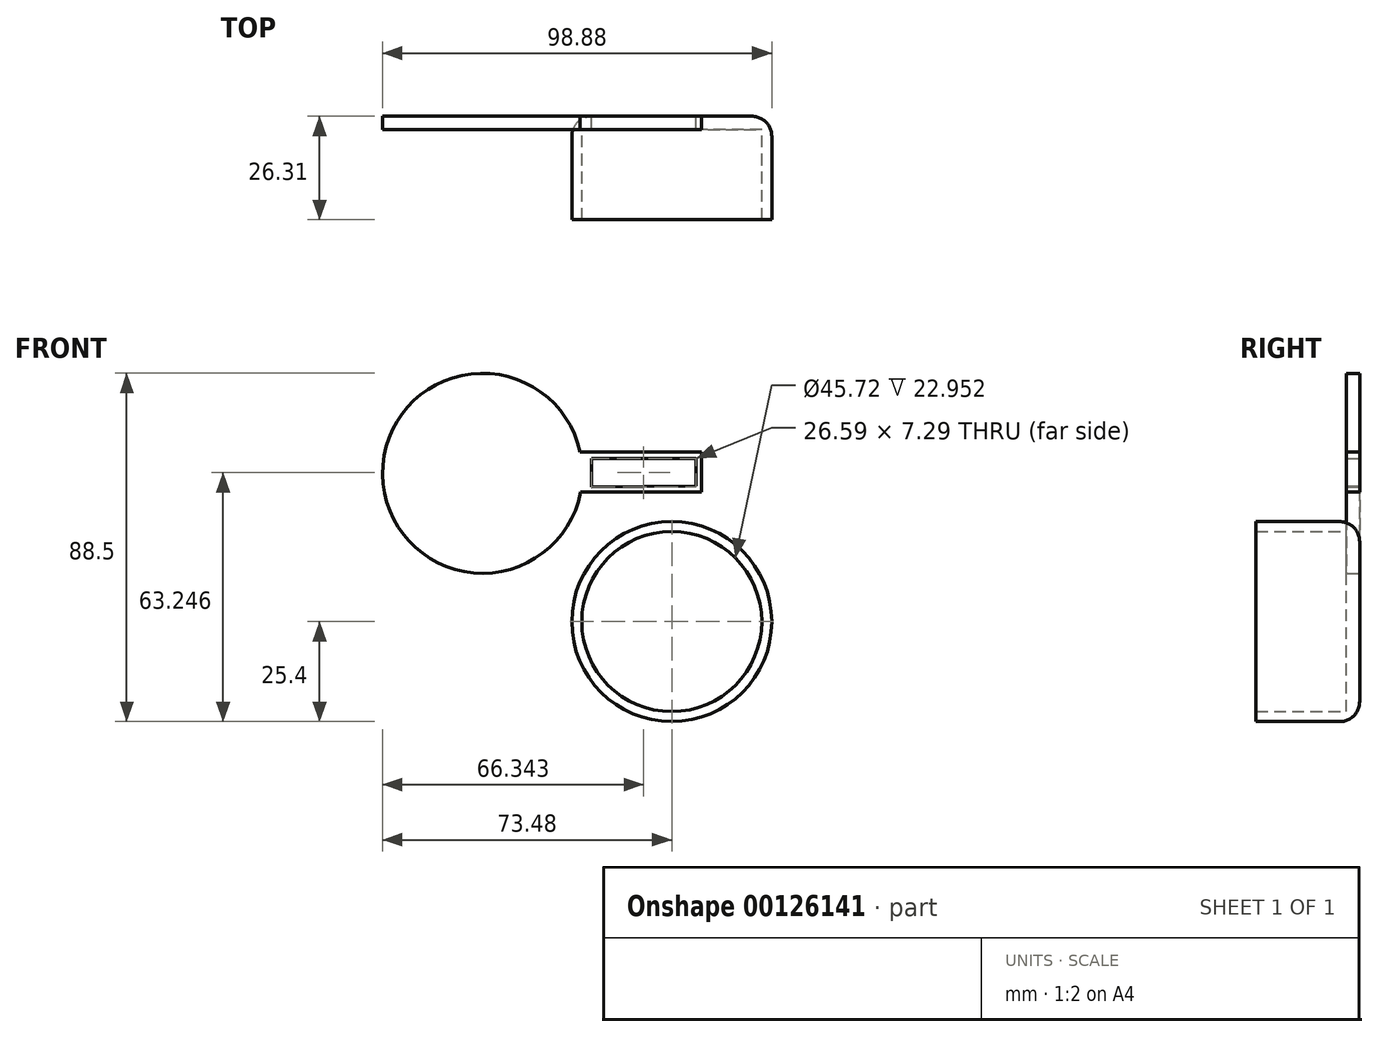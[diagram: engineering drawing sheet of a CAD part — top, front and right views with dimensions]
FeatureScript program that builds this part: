
annotation { "Feature Type Name" : "Feature", "Feature Type Description" : "" }
export const myFeature = defineFeature(function(context is Context, id is Id, definition is map)
    precondition{}
    {
        {
            var Q0;
            Q0=qCreatedBy(makeId("Front.planeOp"),FACE);
            var sketch = newSketch(context, id + "F0", { "sketchPlane" : qUnion([Q0])});
            skCircle(sketch, "E0", {"center": v(0, 0) * mm, "radius": 25.4 * mm});
            skCircle(sketch, "E1", {"center": v(-48.08, 37.7) * mm, "radius": 25.4 * mm});
            skLineSegment(sketch, "E2", {"start": v(-23.26, 43.09) * mm, "end": v(7.54, 43.09) * mm});
            skLineSegment(sketch, "E3", {"start": v(-23.14, 32.9) * mm, "end": v(7.54, 32.9) * mm});
            skLineSegment(sketch, "E4", {"start": v(7.54, 43.09) * mm, "end": v(7.54, 32.9) * mm});
            skLineSegment(sketch, "E5", {"start": v(-20.43, 34.2) * mm, "end": v(-20.43, 41.5) * mm});
            skLineSegment(sketch, "E6", {"start": v(-20.43, 41.5) * mm, "end": v(6.16, 41.5) * mm});
            skLineSegment(sketch, "E7", {"start": v(6.16, 41.5) * mm, "end": v(6.16, 34.46) * mm});
            skLineSegment(sketch, "E8", {"start": v(6.16, 34.46) * mm, "end": v(-20.43, 34.2) * mm});
            skSolve(sketch);
        }
        {
            var Q0;
            Q0=makeQuery(id+"F0.imprint","IMPRINT",FACE,{"disambiguationData":[TD([[makeQuery(id+"F0.imprint","IMPRINT",EDGE,{"derivedFrom":sQuery(id+"F0.wireOp",EDGE,"E0")}),1.0]])]});
            extrude(context, id + "F1", {"entities" : qUnion([Q0]), "depth" : 26.3 * mm});
        }
        {
            var Q0;
            Q0=makeQuery(id+"F1.opExtrude","CAP_FACE",FACE,{"disambiguationData":[OSD([sQuery(id+"F0.wireOp",EDGE,"E0")])],"isStart":false});
            var Q1;
            Q1=makeQuery(id+"F1.opExtrude","SWEPT_BODY",BODY,{"disambiguationData":[OSD([sQuery(id+"F0.wireOp",EDGE,"E0")])]});
            shell(context, id + "F2", {"entities" : qUnion([Q0]), "parts" : qUnion([Q1]), "thickness" : 2.54 * mm});
        }
        {
            var Q0;
            Q0 = qSketchRegion(id + "F0", true);
            extrude(context, id + "F3", {"entities" : qUnion([Q0]), "operationType" : NewBodyOperationType.ADD, "depth" : 3.35 * mm});
        }
        {
            var Q0;
            Q0=makeQuery(id+"F1.opExtrude","CAP_EDGE",EDGE,{"disambiguationData":[OSD([sQuery(id+"F0.wireOp",EDGE,"E0")])],"isStart":true});
            fillet(context, id + "F4", {"entities" : qUnion([Q0]), "radius" : 5.08 * mm, "tangentPropagation" : true, "allowEdgeOverflow" : false});
        }
    });
